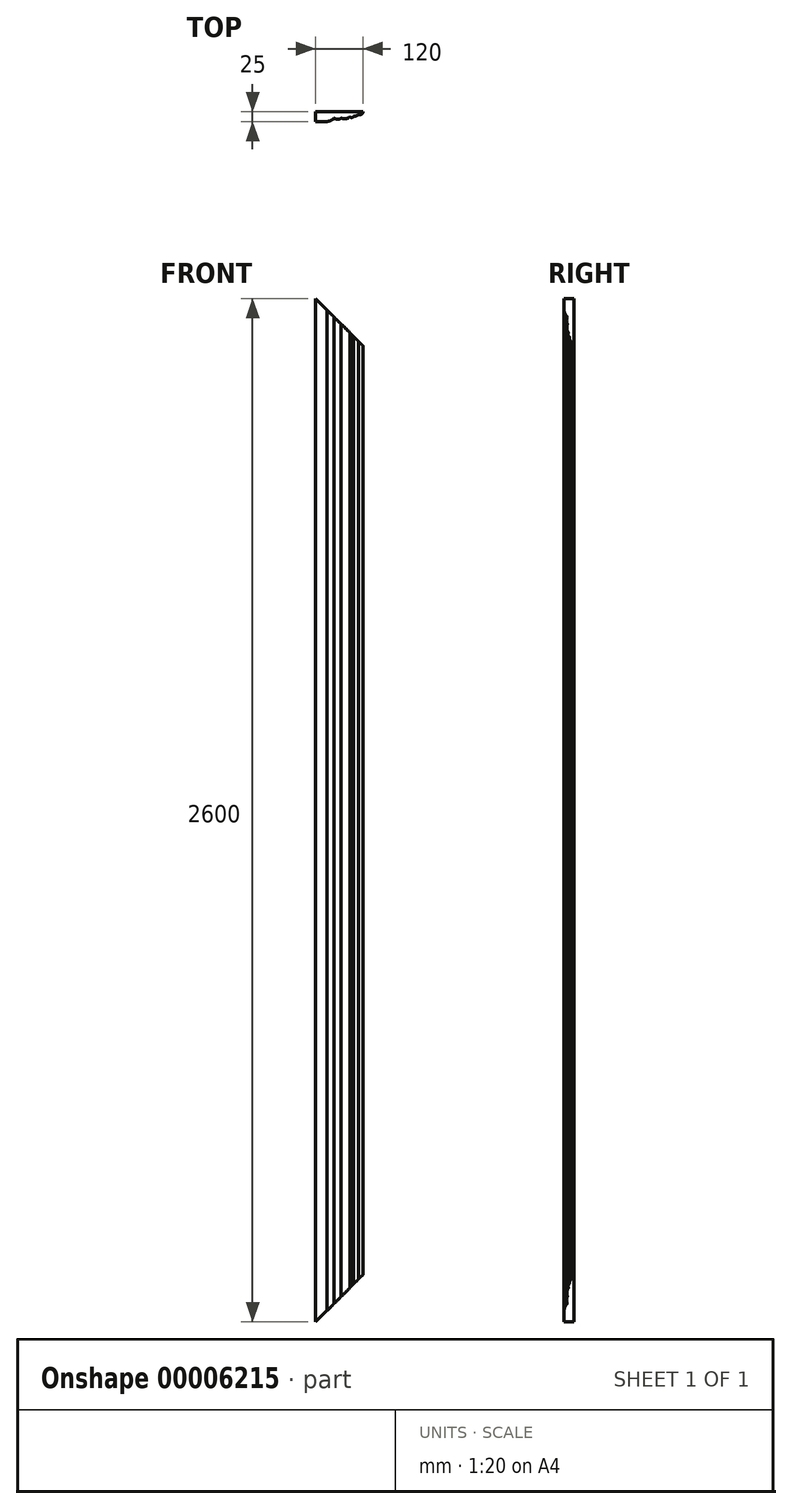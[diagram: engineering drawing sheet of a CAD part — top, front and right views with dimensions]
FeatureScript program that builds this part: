
annotation { "Feature Type Name" : "Feature", "Feature Type Description" : "" }
export const myFeature = defineFeature(function(context is Context, id is Id, definition is map)
    precondition{}
    {
        {
            var Q0;
            Q0=qCreatedBy(makeId("Top.planeOp"),FACE);
            var sketch = newSketch(context, id + "F0", { "sketchPlane" : qUnion([Q0])});
            skLineSegment(sketch, "E0.bottom", {"start": v(0, 0) * mm, "end": v(120, 0) * mm});
            skLineSegment(sketch, "E0.top", {"start": v(0, -25) * mm, "end": v(29.17, -25) * mm});
            skLineSegment(sketch, "E0.left", {"start": v(0, 0) * mm, "end": v(0, -25) * mm});
            skArc(sketch, "E1", {"start": v(29.17, -25) * mm, "mid": v(38.77, -22.24) * mm, "end": v(46.87, -16.4) * mm});
            skArc(sketch, "E2", {"start": v(46.87, -16.4) * mm, "mid": v(55.83, -19.44) * mm, "end": v(64.79, -16.4) * mm});
            skArc(sketch, "E3", {"start": v(64.79, -16.4) * mm, "mid": v(76.31, -17.94) * mm, "end": v(86.98, -13.34) * mm});
            skArc(sketch, "E4", {"start": v(86.98, -13.34) * mm, "mid": v(92.5, -14.89) * mm, "end": v(96.58, -10.84) * mm});
            skArc(sketch, "E5", {"start": v(96.58, -10.84) * mm, "mid": v(103.41, -10.57) * mm, "end": v(109.18, -6.9) * mm});
            skArc(sketch, "E6", {"start": v(109.18, -6.9) * mm, "mid": v(116.48, -6.42) * mm, "end": v(120, 0) * mm});
            skSolve(sketch);
        }
        {
            var Q0;
            Q0=makeQuery(id+"F0.imprint","IMPRINT",FACE,{"disambiguationData":[TD([[makeQuery(id+"F0.imprint","IMPRINT",EDGE,{"derivedFrom":sQuery(id+"F0.wireOp",EDGE,"E0.bottom")}),-1.0]])]});
            extrude(context, id + "F1", {"entities" : qUnion([Q0]), "depth" : 2600 * mm});
        }
        {
            var Q0;
            Q0=makeQuery(id+"F1.opExtrude","SWEPT_FACE",FACE,{"disambiguationData":[OSD([sQuery(id+"F0.wireOp",EDGE,"E0.bottom")])]});
            var sketch = newSketch(context, id + "F2", { "sketchPlane" : qUnion([Q0])});
            skLineSegment(sketch, "E7", {"start": v(0, 0) * mm, "end": v(-120, 120) * mm});
            skLineSegment(sketch, "E8", {"start": v(0, 2600) * mm, "end": v(-120, 2480) * mm});
            skLineSegment(sketch, "E9", {"start": v(-120, 120) * mm, "end": v(-120, 0) * mm});
            skLineSegment(sketch, "E10", {"start": v(-120, 0) * mm, "end": v(0, 0) * mm});
            skLineSegment(sketch, "E11", {"start": v(0, 2600) * mm, "end": v(-120, 2600) * mm});
            skLineSegment(sketch, "E12", {"start": v(-120, 2600) * mm, "end": v(-120, 2480) * mm});
            skSolve(sketch);
        }
        {
            var Q0;
            Q0 = qSketchRegion(id + "F2", true);
            extrude(context, id + "F3", {"entities" : qUnion([Q0]), "operationType" : NewBodyOperationType.REMOVE, "oppositeDirection" : true, "depth" : 25 * mm});
        }
    });
